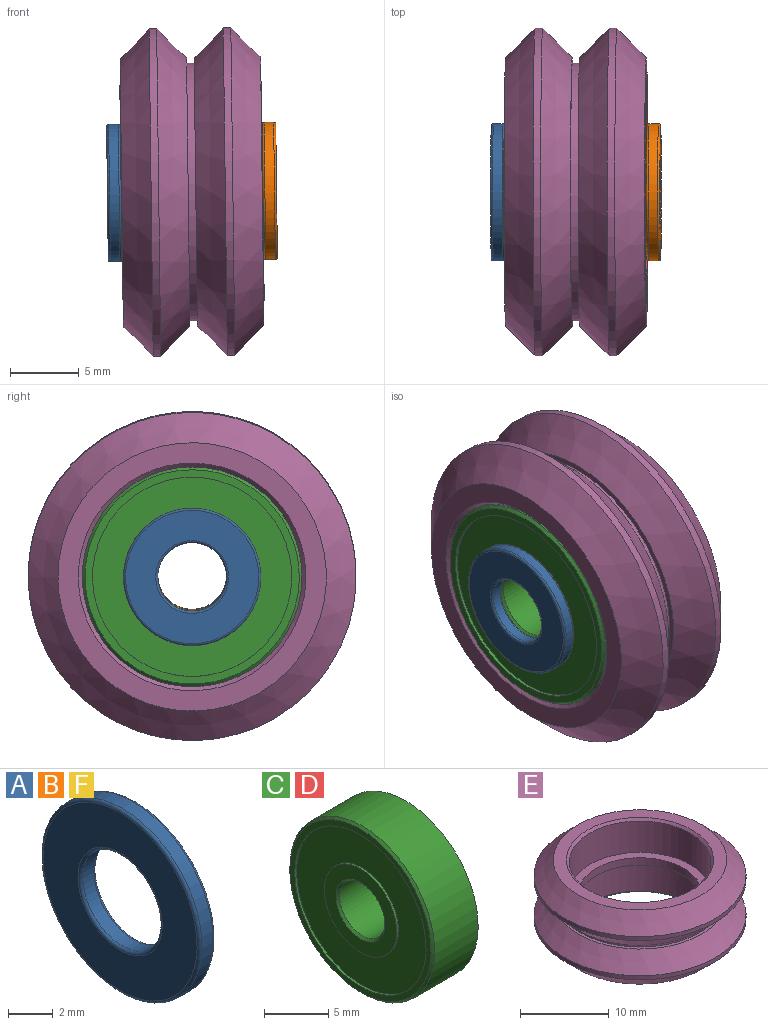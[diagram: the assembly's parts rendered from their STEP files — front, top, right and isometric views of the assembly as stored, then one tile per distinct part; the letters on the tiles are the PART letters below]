
ASSEMBLY  parts=6 mates=5
PART A: 8 faces, bbox 1x10.8x10.8 mm
  f0: torus R=4.85mm, axis (1,0,0), area 7.3mm2, adj f5,f6
  f1: torus R=2.65mm, axis (1,0,0), area 3.8mm2, adj f4,f6
  f2: torus R=4.85mm, axis (1,0,0), area 7.3mm2, adj f5,f7
  f3: torus R=2.65mm, axis (1,0,0), area 3.8mm2, adj f4,f7
  f4: cylinder r=2.5mm len=5mm, axis (-1,0,0), area 11mm2, adj f1,f3
  f5: cylinder r=5mm len=10mm, axis (-1,0,0), area 22mm2, adj f0,f2
  f6: plane 9.7x9.7mm, normal (1,0,0), area 51.8mm2, adj f0,f1
  f7: plane 9.7x9.7mm, normal (-1,0,0), area 51.8mm2, adj f2,f3
PART B: same geometry as A
PART C: 15 faces, bbox 5x16x16 mm
  f0: cone r=8mm half-angle=45deg, axis (1,0,0), area 14mm2, adj f8,f9
  f1: cone r=2.7mm half-angle=45deg, axis (-1,0,0), area 4.6mm2, adj f7,f12
  f2: cone r=2.5mm half-angle=45deg, axis (1,0,0), area 4.6mm2, adj f7,f10
  f3: cone r=7.25mm half-angle=45deg, axis (1,0,0), area 13.1mm2, adj f11,f13
  f4: cylinder r=4mm len=8mm, axis (-1,0,0), area 5mm2, adj f12,f14
  f5: cylinder r=7.25mm len=14.5mm, axis (-1,0,0), area 9.1mm2, adj f9,f14
  f6: cylinder r=4mm len=8mm, axis (1,0,0), area 5mm2, adj f10,f13
  f7: cylinder r=2.5mm len=5mm, axis (1,0,0), area 72.3mm2, adj f1,f2
  f8: cylinder r=8mm len=16mm, axis (-1,0,0), area 241.3mm2, adj f0,f11
  f9: plane 15.6x15.6mm, normal (-1,0,0), area 26mm2, adj f0,f5
  f10: plane 8x8mm, normal (1,0,0), area 27.4mm2, adj f2,f6
  f11: plane 16x16mm, normal (1,0,0), area 26.7mm2, adj f3,f8
  f12: plane 8x8mm, normal (-1,0,0), area 27.4mm2, adj f1,f4
  f13: plane 14.5x14.5mm, normal (1,0,0), area 114.9mm2, adj f3,f6
  f14: plane 14.5x14.5mm, normal (-1,0,0), area 114.9mm2, adj f4,f5
PART D: same geometry as C
PART E: 18 faces, bbox 23.9x23.9x10.2 mm
  f0: cone r=8.29mm half-angle=45deg, axis (0,0,1), area 21.7mm2, adj f3,f15
  f1: cone r=7.99mm half-angle=45deg, axis (0,0,-1), area 21.7mm2, adj f11,f12
  f2: cylinder r=6.94mm len=13.89mm, axis (0,0,-1), area 43.6mm2, adj f16,f17
  f3: cylinder r=7.99mm len=15.97mm, axis (0,0,-1), area 216.5mm2, adj f0,f16
  f4: cone r=9.77mm half-angle=45.5deg, axis (0,0,-1), area 208.2mm2, adj f5,f15
  f5: cylinder r=11.95mm len=23.89mm, axis (0,0,-1), area 41.3mm2, adj f4,f6
  f6: cone r=11.95mm half-angle=45.3deg, axis (0,0,1), area 208.6mm2, adj f5,f14
  f7: cylinder r=9.38mm len=18.75mm, axis (0,0,-1), area 32.4mm2, adj f13,f14
  f8: cone r=9.77mm half-angle=45.3deg, axis (0,0,-1), area 208.6mm2, adj f9,f13
  f9: cylinder r=11.95mm len=23.89mm, axis (0,0,-1), area 41.3mm2, adj f8,f10
  f10: cone r=11.95mm half-angle=45.5deg, axis (0,0,1), area 208.2mm2, adj f9,f12
  f11: cylinder r=7.99mm len=15.97mm, axis (0,0,-1), area 216.5mm2, adj f1,f17
  f12: plane 19.54x19.54mm, normal (0,0,-1), area 84.1mm2, adj f1,f10
  f13: plane 19.54x19.54mm, normal (0,0,1), area 23.8mm2, adj f7,f8
  f14: plane 19.54x19.54mm, normal (0,0,-1), area 23.8mm2, adj f6,f7
  f15: plane 19.54x19.54mm, normal (0,0,1), area 84.1mm2, adj f0,f4
  f16: plane 15.97x15.97mm, normal (0,0,1), area 48.9mm2, adj f2,f3
  f17: plane 15.97x15.97mm, normal (0,0,-1), area 48.9mm2, adj f2,f11
PART F: same geometry as A
PLACE A rot(axis=(0,-1,0),0.7deg) t=(30.16,-3.35,3.26)mm
PLACE B rot(axis=(0,-1,0),0.7deg) t=(41.47,-3.35,3.4)mm
PLACE C rot(axis=(0,-1,0),0.7deg) t=(33.66,-3.35,3.31)mm
PLACE D rot(axis=(0,-1,0),0.7deg) t=(38.97,-3.35,3.37)mm
PLACE E rot(axis=(0,-1,0),90.7deg) t=(36.32,-3.35,3.34)mm
PLACE F rot(axis=(0,-1,0),0.7deg) t=(35.82,-3.35,3.33)mm
MATE fastened A.f0 <-> C.f0  axis (1,0,0.01) through (31.16,-3.35,3.27)mm
MATE fastened D.f0 <-> E.f3  axis (1,0,0.01) through (38.97,-3.35,3.37)mm
MATE fastened F.f0 <-> E.f2  axis (-1,0,-0.01) through (36.32,-3.35,3.34)mm
MATE fastened C.f0 <-> E.f3  axis (1,0,0.01) through (33.66,-3.35,3.31)mm
MATE fastened B.f0 <-> D.f0  axis (-1,0,-0.01) through (41.47,-3.35,3.4)mm
